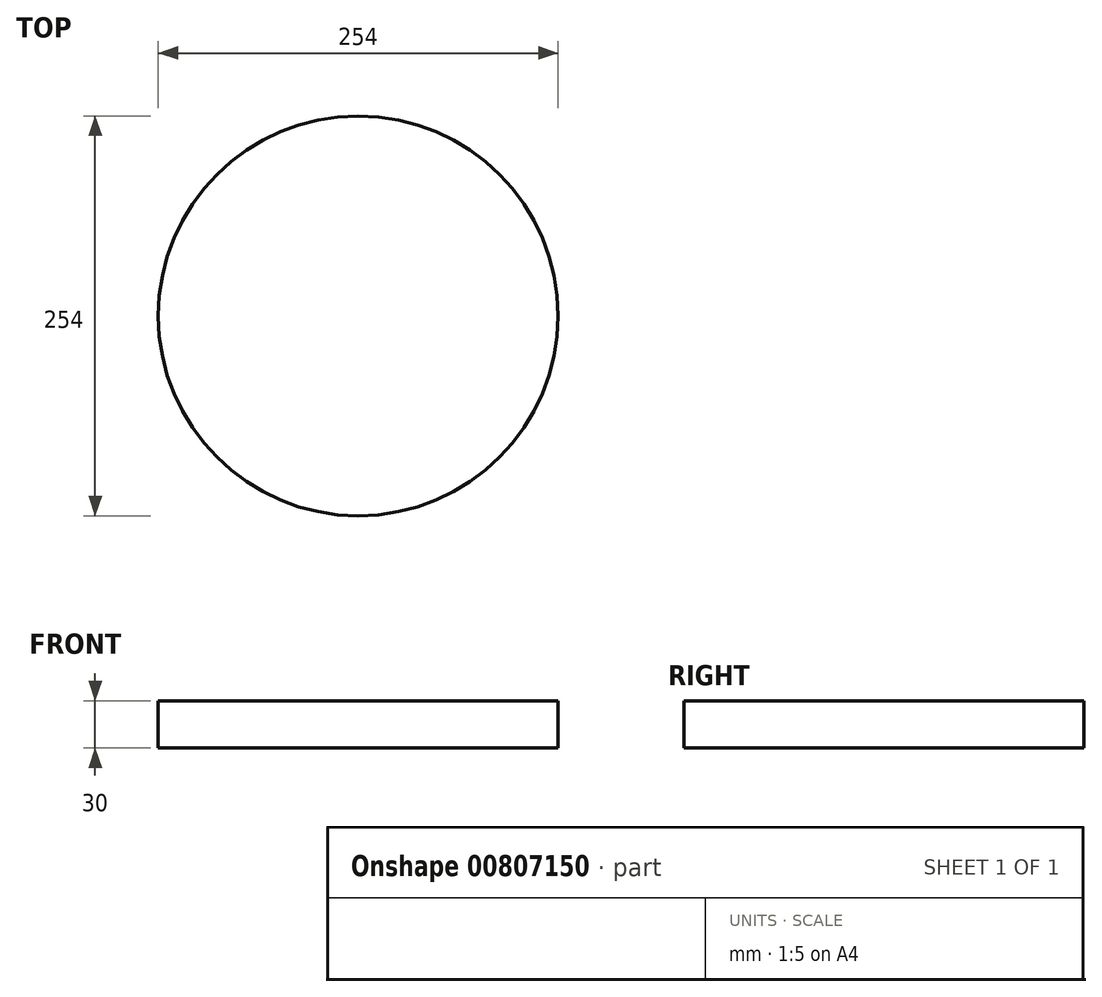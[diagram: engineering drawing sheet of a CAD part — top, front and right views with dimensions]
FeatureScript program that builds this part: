
annotation { "Feature Type Name" : "Feature", "Feature Type Description" : "" }
export const myFeature = defineFeature(function(context is Context, id is Id, definition is map)
    precondition{}
    {
        {
            var Q0;
            Q0=qCreatedBy(makeId("Top.planeOp"),FACE);
            var sketch = newSketch(context, id + "F0", { "sketchPlane" : qUnion([Q0])});
            skCircle(sketch, "E0", {"center": v(0, 0) * mm, "radius": 127 * mm});
            skSolve(sketch);
        }
        {
            var Q0;
            Q0=qSketchRegion(id+"F0",true);
            extrude(context, id + "F1", {"entities" : qUnion([Q0]), "depth" : 30 * mm, "offsetDistance" : 25.4 * mm});
        }
    });
